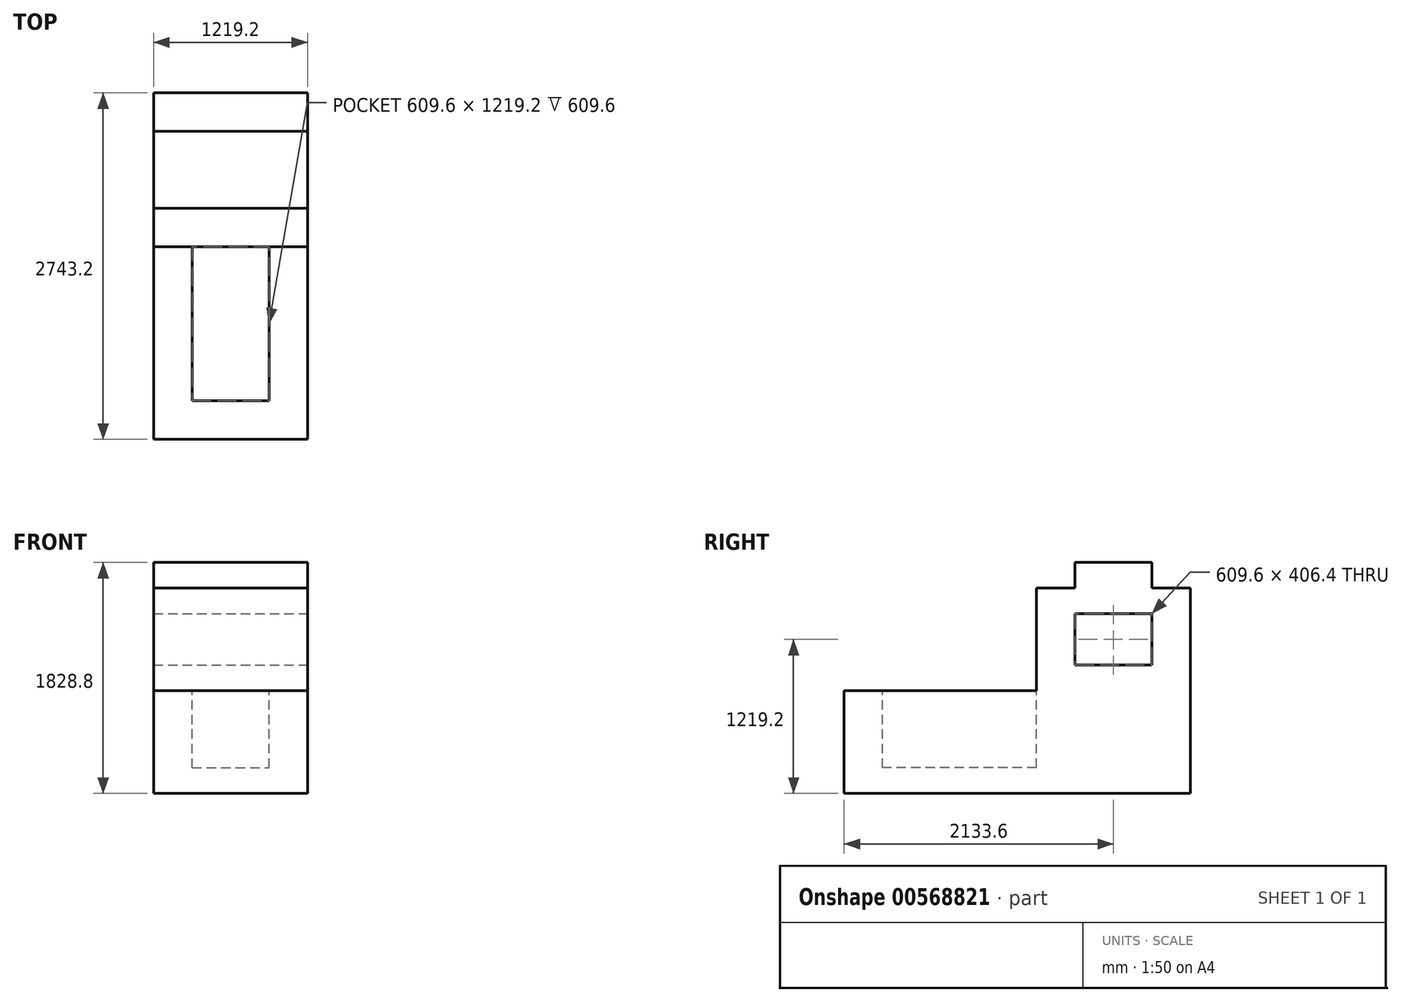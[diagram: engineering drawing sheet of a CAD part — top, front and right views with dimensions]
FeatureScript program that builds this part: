
annotation { "Feature Type Name" : "Feature", "Feature Type Description" : "" }
export const myFeature = defineFeature(function(context is Context, id is Id, definition is map)
    precondition{}
    {
        {
            var Q0;
            Q0=qCreatedBy(makeId("Right.planeOp"),FACE);
            var sketch = newSketch(context, id + "F0", { "sketchPlane" : qUnion([Q0])});
            skLineSegment(sketch, "E0", {"start": v(0, 0) * mm, "end": v(-2743.2, 0) * mm});
            skLineSegment(sketch, "E1", {"start": v(-2743.2, 0) * mm, "end": v(-2743.2, 812.8) * mm});
            skLineSegment(sketch, "E2", {"start": v(-2743.2, 812.8) * mm, "end": v(-1219.2, 812.8) * mm});
            skLineSegment(sketch, "E3", {"start": v(-1219.2, 812.8) * mm, "end": v(-1219.2, 1625.6) * mm});
            skLineSegment(sketch, "E4", {"start": v(-1219.2, 1625.6) * mm, "end": v(-914.4, 1625.6) * mm});
            skLineSegment(sketch, "E5", {"start": v(-914.4, 1625.6) * mm, "end": v(-914.4, 1828.8) * mm});
            skLineSegment(sketch, "E6", {"start": v(-914.4, 1828.8) * mm, "end": v(-304.8, 1828.8) * mm});
            skLineSegment(sketch, "E7", {"start": v(-304.8, 1828.8) * mm, "end": v(-304.8, 1625.6) * mm});
            skLineSegment(sketch, "E8", {"start": v(-304.8, 1625.6) * mm, "end": v(0, 1625.6) * mm});
            skLineSegment(sketch, "E9", {"start": v(0, 1625.6) * mm, "end": v(0, 0) * mm});
            skLineSegment(sketch, "E10", {"start": v(-914.4, 1422.4) * mm, "end": v(-304.8, 1422.4) * mm});
            skLineSegment(sketch, "E11", {"start": v(-304.8, 1422.4) * mm, "end": v(-304.8, 1016) * mm});
            skLineSegment(sketch, "E12", {"start": v(-304.8, 1016) * mm, "end": v(-914.4, 1016) * mm});
            skLineSegment(sketch, "E13", {"start": v(-914.4, 1016) * mm, "end": v(-914.4, 1422.4) * mm});
            skSolve(sketch);
        }
        {
            var Q0;
            Q0 = qSketchRegion(id + "F0", true);
            extrude(context, id + "F1", {"entities" : qUnion([Q0]), "oppositeDirection" : true, "depth" : 1219.2 * mm, "offsetDistance" : 25.4 * mm});
        }
        {
            var Q0;
            Q0=makeQuery(id+"F1.opExtrude","SWEPT_FACE",FACE,{"disambiguationData":[OSD([sQuery(id+"F0.wireOp",EDGE,"E2")])]});
            var sketch = newSketch(context, id + "F2", { "sketchPlane" : qUnion([Q0])});
            skLineSegment(sketch, "E14", {"start": v(0, -1219.2) * mm, "end": v(-304.8, -1219.2) * mm});
            skLineSegment(sketch, "E15", {"start": v(-304.8, -1219.2) * mm, "end": v(-304.8, -2438.4) * mm});
            skLineSegment(sketch, "E16", {"start": v(-304.8, -2438.4) * mm, "end": v(-914.4, -2438.4) * mm});
            skLineSegment(sketch, "E17", {"start": v(-914.4, -2438.4) * mm, "end": v(-914.4, -1219.2) * mm});
            skSolve(sketch);
        }
        {
            var Q0;
            {var subQ0=sQuery(id+"F2.wireOp",EDGE,"E15");Q0=makeQuery(id+"F2.imprint","IMPRINT",FACE,{"disambiguationData":[TD([[makeQuery(id+"F2.imprint","IMPRINT",EDGE,{"derivedFrom":subQ0}),-1.0]])]});}
            extrude(context, id + "F3", {"entities" : qUnion([Q0]), "operationType" : NewBodyOperationType.REMOVE, "oppositeDirection" : true, "depth" : 609.6 * mm, "offsetDistance" : 25.4 * mm});
        }
    });
